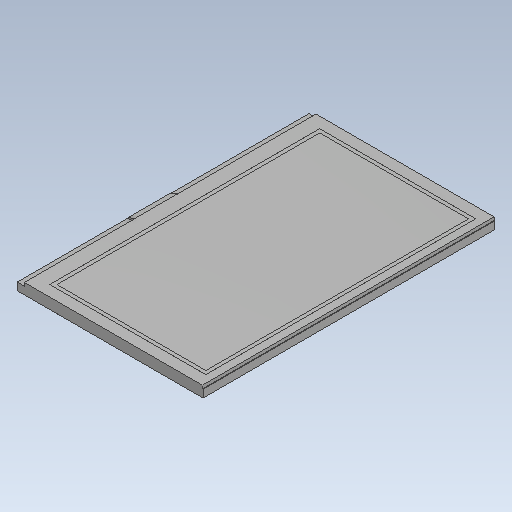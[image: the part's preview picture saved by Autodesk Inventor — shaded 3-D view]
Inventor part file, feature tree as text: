
AUTODESK INVENTOR PART (.ipt)
format: ipt  version: 2020 (Build 240168000, 168)  size: 104,960 bytes
history: native  units: in
note: dims shown in document units (in); Inventor stores cm internally (conversion verified against a paired STEP export)
features: chamfer x1
ambient origin geometry x8: Origin, YZ Plane, XZ Plane, XY Plane, X Axis, Y Axis, Z Axis, Center Point
bodies: Solid1 (feature_tree)
feature tree (1):
  chamfer  "Chamfer2"  [1 undecoded]
note: 1 required parameter value undecoded (feature->parameter linkage not recoverable at this tier; creation-order binding heuristic only, values carry confidence <= 0.55)
